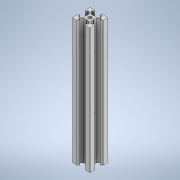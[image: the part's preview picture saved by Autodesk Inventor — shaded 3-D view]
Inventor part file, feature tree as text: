
AUTODESK INVENTOR PART (.ipt)
format: ipt  version: 2021 (Build 250183000, 183)  size: 283,136 bytes
history: native  units: mm
features: sketch x4, extrude x2, fillet x2, hole x2, other x1, pattern_circular x1, projected_geometry x1
ambient origin geometry x8: Origin, YZ Plane, XZ Plane, XY Plane, X Axis, Y Axis, Z Axis, Center Point
bodies: Body1 (feature_tree)
feature tree (13):
  other  "實體1"
  extrude  "擠出1"  Depth=20.0mm
  extrude  "擠出2"  Depth=20.0mm
  fillet  "圓角1"  Radius=142.0mm
  pattern_circular  "環形陣列1"  [2 undecoded]
  hole  "孔1"  [1 undecoded]
  fillet  "圓角2"  Radius=6.2mm
  hole  "孔2"  [1 undecoded]
  sketch  "草圖1"
  sketch  "草圖2"
  projected_geometry  "投影迴路1"
  sketch  "草圖3"
  sketch  "草圖4"
note: 4 required parameter values undecoded (feature->parameter linkage not recoverable at this tier; creation-order binding heuristic only, values carry confidence <= 0.55)
